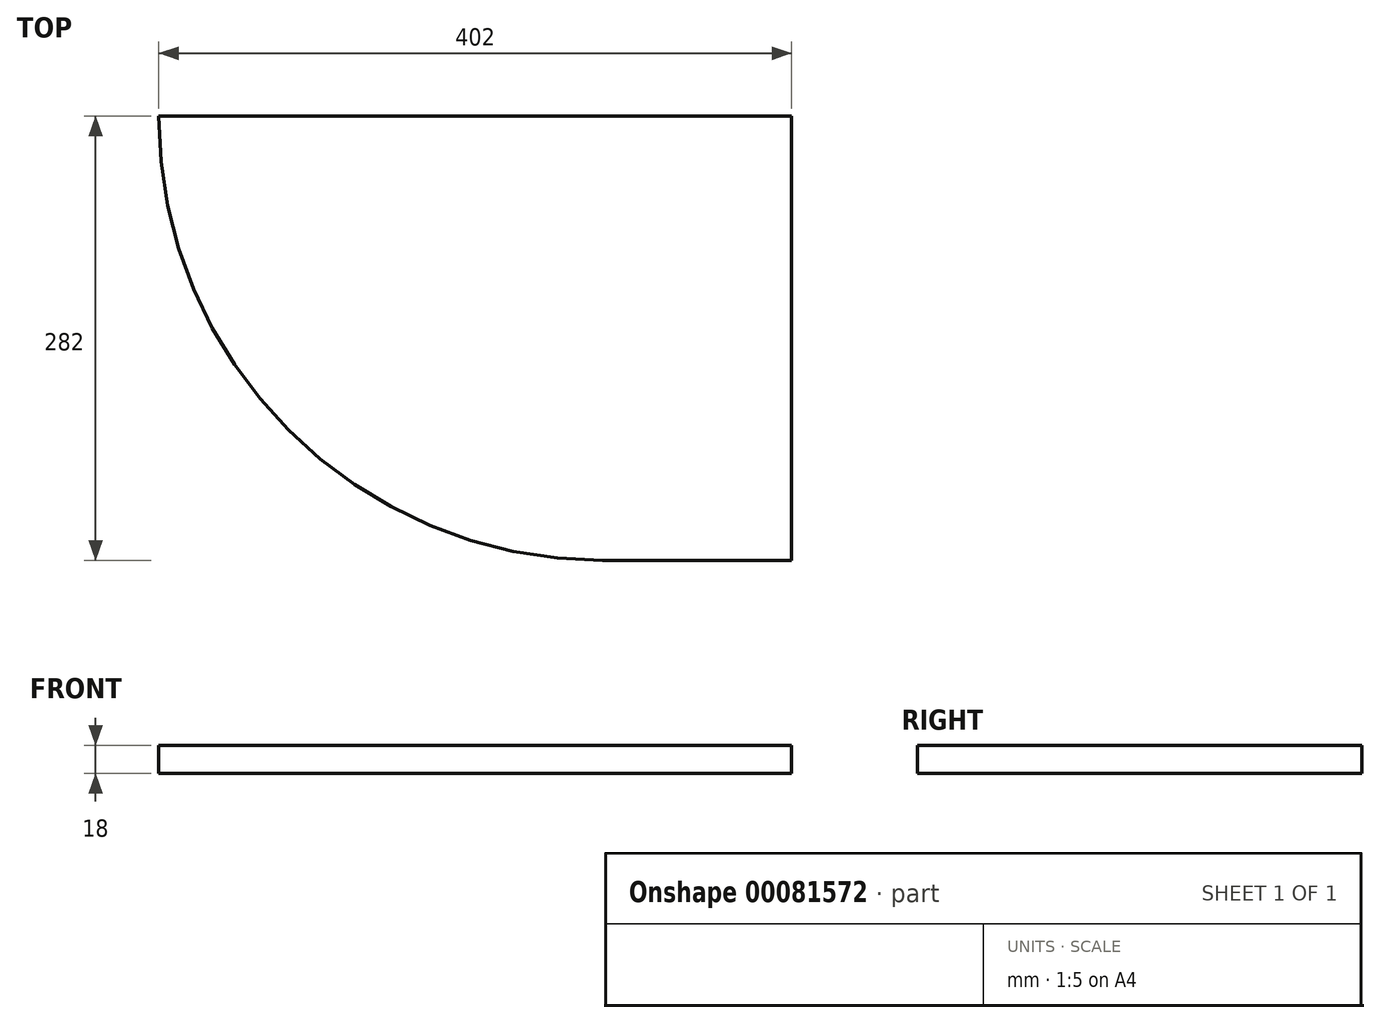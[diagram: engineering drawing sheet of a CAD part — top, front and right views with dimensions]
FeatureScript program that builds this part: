
annotation { "Feature Type Name" : "Feature", "Feature Type Description" : "" }
export const myFeature = defineFeature(function(context is Context, id is Id, definition is map)
    precondition{}
    {
        {
            var Q0;
            Q0=qCreatedBy(makeId("Top.planeOp"),FACE);
            var sketch = newSketch(context, id + "F0", { "sketchPlane" : qUnion([Q0])});
            skLineSegment(sketch, "E0.bottom", {"start": v(282, 0) * mm, "end": v(402, 0) * mm});
            skLineSegment(sketch, "E0.top", {"start": v(0, 282) * mm, "end": v(402, 282) * mm});
            skLineSegment(sketch, "E0.left", {"start": v(0, 282) * mm, "end": v(0, 282) * mm});
            skLineSegment(sketch, "E0.right", {"start": v(402, 0) * mm, "end": v(402, 282) * mm});
            skPoint(sketch, "E1.visualSharp", {"position": v(0, 0) * mm});
            skArc(sketch, "E1.filletArc", {"start": v(0, 282) * mm, "mid": v(82.6, 82.6) * mm, "end": v(282, 0) * mm});
            skSolve(sketch);
        }
        {
            var Q0;
            Q0 = qSketchRegion(id + "F0", true);
            extrude(context, id + "F1", {"entities" : qUnion([Q0]), "depth" : 18 * mm});
        }
    });
